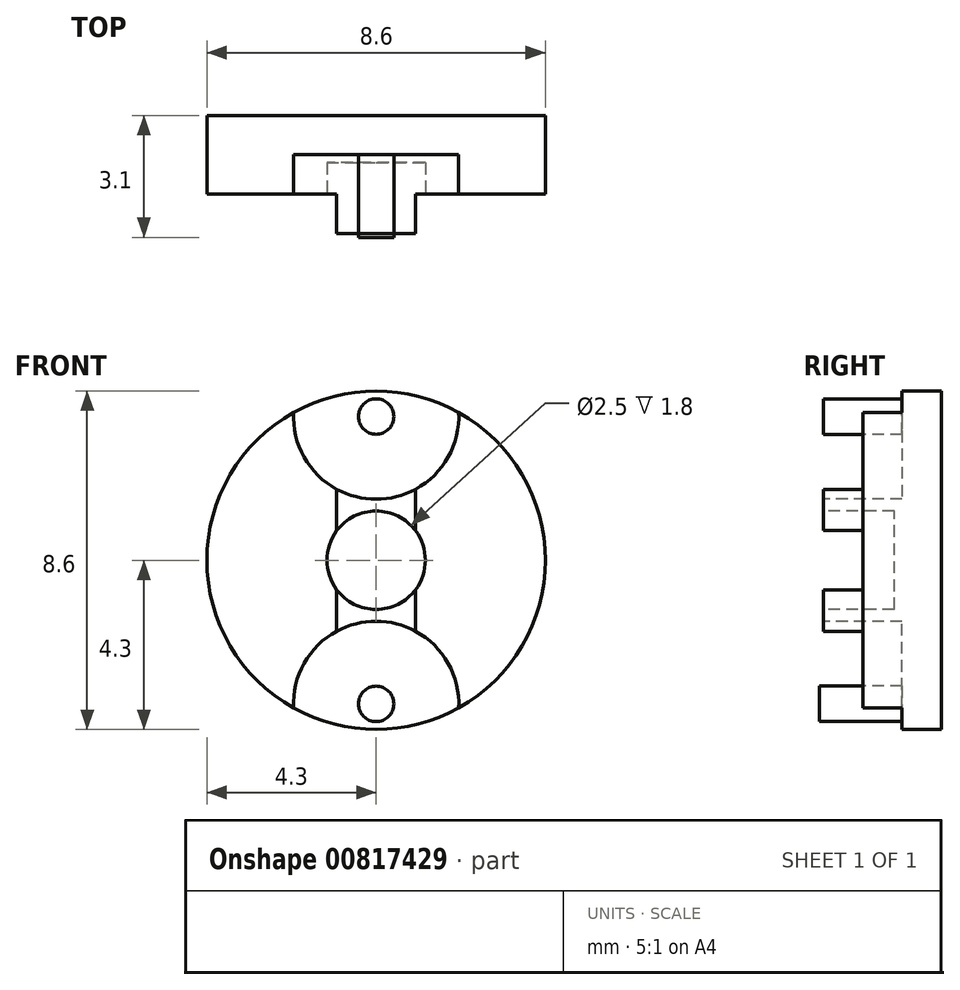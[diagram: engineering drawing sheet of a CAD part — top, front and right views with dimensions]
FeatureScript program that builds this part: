
annotation { "Feature Type Name" : "Feature", "Feature Type Description" : "" }
export const myFeature = defineFeature(function(context is Context, id is Id, definition is map)
    precondition{}
    {
        {
            var Q0;
            Q0=qCreatedBy(makeId("Front.planeOp"),FACE);
            var sketch = newSketch(context, id + "F0", { "sketchPlane" : qUnion([Q0])});
            skCircle(sketch, "E0", {"center": v(0, 0) * mm, "radius": 4.3 * mm});
            skSolve(sketch);
        }
        {
            var Q0;
            Q0=makeQuery(id+"F0.imprint","IMPRINT",FACE,{"disambiguationData":[TD([[makeQuery(id+"F0.imprint","IMPRINT",EDGE,{"derivedFrom":sQuery(id+"F0.wireOp",EDGE,"E0")}),1.0]])]});
            extrude(context, id + "F1", {"entities" : qUnion([Q0]), "depth" : 3 * mm, "offsetDistance" : 25 * mm});
        }
        {
            var Q0;
            Q0=makeQuery(id+"F1.opExtrude","CAP_FACE",FACE,{"disambiguationData":[OSD([sQuery(id+"F0.wireOp",EDGE,"E0")])],"isStart":false});
            var sketch = newSketch(context, id + "F2", { "sketchPlane" : qUnion([Q0])});
            skCircle(sketch, "E1", {"center": v(0, 3.65) * mm, "radius": 2.1 * mm});
            skCircle(sketch, "E2", {"center": v(0, 3.65) * mm, "radius": 0.45 * mm});
            skPoint(sketch, "E3.center", {"position": v(0, 0) * mm});
            skCircle(sketch, "E4.1.0", {"center": v(0, -3.65) * mm, "radius": 0.45 * mm});
            skCircle(sketch, "E4.1.1", {"center": v(0, -3.65) * mm, "radius": 2.1 * mm});
            skLineSegment(sketch, "E5", {"start": v(-2.1, -3.75) * mm, "end": v(-2.1, -3.75) * mm});
            skCircle(sketch, "E6.1.0", {"center": v(0, -3.65) * mm, "radius": 0.75 * mm});
            skLineSegment(sketch, "E7", {"start": v(-1, 4.18) * mm, "end": v(-1, -4.18) * mm});
            skLineSegment(sketch, "E8.MirrorCS", {"start": v(1, 4.18) * mm, "end": v(1, -4.18) * mm});
            skSolve(sketch);
        }
        {
            var Q0;
            Q0=makeQuery(id+"F2.imprint","IMPRINT",FACE,{"disambiguationData":[TD([[makeQuery(id+"F2.imprint","IMPRINT",EDGE,{"derivedFrom":sQuery(id+"F2.wireOp",EDGE,"E4.1.0")}),-1.0]])]});
            var Q1;
            Q1=makeQuery(id+"F2.imprint","IMPRINT",FACE,{"disambiguationData":[TD([[makeQuery(id+"F2.imprint","IMPRINT",EDGE,{"derivedFrom":sQuery(id+"F2.wireOp",EDGE,"E4.2.0")}),-1.0]])]});
            var Q2;
            Q2=makeQuery(id+"F2.imprint","IMPRINT",FACE,{"disambiguationData":[TD([[makeQuery(id+"F2.imprint","IMPRINT",EDGE,{"derivedFrom":sQuery(id+"F2.wireOp",EDGE,"E2")}),-1.0]])]});
            var Q3;
            {var subQ0=sQuery(id+"F2.wireOp",EDGE,"72799f41-8f97-4659-aa58-32a5e735416f.0");var subQ1=sQuery(id+"F2.wireOp",EDGE,"E1");var subQ2=makeQuery(id+"F2.imprint","INTERSECT",VERTEX,{"derivedFrom":[subQ1,subQ0]});Q3=makeQuery(id+"F2.imprint","IMPRINT",FACE,{"disambiguationData":[TD([[makeQuery(id+"F2.imprint","IMPRINT",EDGE,{"disambiguationData":[TD([[subQ2,1.0]])],"derivedFrom":subQ1}),1.0]])]});}
            var Q4;
            {var subQ0=sQuery(id+"F2.wireOp",EDGE,"244a7301-85a8-4d62-895f-e92157d3d9ef.0");var subQ1=sQuery(id+"F2.wireOp",EDGE,"E1");var subQ2=makeQuery(id+"F2.imprint","INTERSECT",VERTEX,{"derivedFrom":[subQ1,subQ0]});Q4=makeQuery(id+"F2.imprint","IMPRINT",FACE,{"disambiguationData":[TD([[makeQuery(id+"F2.imprint","IMPRINT",EDGE,{"disambiguationData":[TD([[subQ2,-1.0]])],"derivedFrom":subQ1}),1.0]])]});}
            var Q5;
            {var subQ0=sQuery(id+"F2.wireOp",EDGE,"244a7301-85a8-4d62-895f-e92157d3d9ef.0");var subQ1=sQuery(id+"F2.wireOp",EDGE,"E4.2.1");var subQ2=makeQuery(id+"F2.imprint","INTERSECT",VERTEX,{"derivedFrom":[subQ1,subQ0]});Q5=makeQuery(id+"F2.imprint","IMPRINT",FACE,{"disambiguationData":[TD([[makeQuery(id+"F2.imprint","IMPRINT",EDGE,{"disambiguationData":[TD([[subQ2,1.0]])],"derivedFrom":subQ1}),1.0]])]});}
            var Q6;
            {var subQ0=sQuery(id+"F2.wireOp",EDGE,"b240cd5d-7871-482e-b949-4fee4bfa505a.0");var subQ1=sQuery(id+"F2.wireOp",EDGE,"E4.2.1");var subQ2=makeQuery(id+"F2.imprint","INTERSECT",VERTEX,{"derivedFrom":[subQ1,subQ0]});Q6=makeQuery(id+"F2.imprint","IMPRINT",FACE,{"disambiguationData":[TD([[makeQuery(id+"F2.imprint","IMPRINT",EDGE,{"disambiguationData":[TD([[subQ2,-1.0]])],"derivedFrom":subQ1}),1.0]])]});}
            var Q7;
            {var subQ0=sQuery(id+"F2.wireOp",EDGE,"b240cd5d-7871-482e-b949-4fee4bfa505a.0");var subQ1=sQuery(id+"F2.wireOp",EDGE,"E4.1.1");var subQ2=makeQuery(id+"F2.imprint","INTERSECT",VERTEX,{"derivedFrom":[subQ1,subQ0]});Q7=makeQuery(id+"F2.imprint","IMPRINT",FACE,{"disambiguationData":[TD([[makeQuery(id+"F2.imprint","IMPRINT",EDGE,{"disambiguationData":[TD([[subQ2,1.0]])],"derivedFrom":subQ1}),1.0]])]});}
            var Q8;
            {var subQ0=sQuery(id+"F2.wireOp",EDGE,"72799f41-8f97-4659-aa58-32a5e735416f.0");var subQ1=sQuery(id+"F2.wireOp",EDGE,"E4.1.1");var subQ2=makeQuery(id+"F2.imprint","INTERSECT",VERTEX,{"derivedFrom":[subQ1,subQ0]});Q8=makeQuery(id+"F2.imprint","IMPRINT",FACE,{"disambiguationData":[TD([[makeQuery(id+"F2.imprint","IMPRINT",EDGE,{"disambiguationData":[TD([[subQ2,-1.0]])],"derivedFrom":subQ1}),1.0]])]});}
            var Q9;
            Q9=makeQuery(id+"F2.imprint","IMPRINT",FACE,{"disambiguationData":[TD([[makeQuery(id+"F2.imprint","IMPRINT",EDGE,{"derivedFrom":sQuery(id+"F2.wireOp",EDGE,"E6.1.0")}),-1.0]])]});
            var Q10;
            Q10=makeQuery(id+"F2.imprint","IMPRINT",FACE,{"disambiguationData":[TD([[makeQuery(id+"F2.imprint","IMPRINT",EDGE,{"derivedFrom":sQuery(id+"F2.wireOp",EDGE,"E6.2.0")}),-1.0]])]});
            var Q11;
            Q11=makeQuery(id+"F2.imprint","IMPRINT",FACE,{"disambiguationData":[TD([[makeQuery(id+"F2.imprint","IMPRINT",EDGE,{"derivedFrom":sQuery(id+"F2.wireOp",EDGE,"HzP3ErbT-1h8t-Fggi-4kVG-w2r0vP4Ld2Wb")}),-1.0]])]});
            var Q12;
            {var subQ0=sQuery(id+"F2.wireOp",EDGE,"b240cd5d-7871-482e-b949-4fee4bfa505a.0");var subQ1=sQuery(id+"F2.wireOp",EDGE,"E4.1.1");var subQ2=makeQuery(id+"F2.imprint","INTERSECT",VERTEX,{"derivedFrom":[subQ1,subQ0]});Q12=makeQuery(id+"F2.imprint","IMPRINT",FACE,{"disambiguationData":[TD([[makeQuery(id+"F2.imprint","IMPRINT",EDGE,{"disambiguationData":[TD([[subQ2,-1.0]])],"derivedFrom":subQ1}),1.0]])]});}
            var Q13;
            {var subQ0=sQuery(id+"F2.wireOp",EDGE,"244a7301-85a8-4d62-895f-e92157d3d9ef.0");var subQ1=sQuery(id+"F2.wireOp",EDGE,"E4.1.1");var subQ2=makeQuery(id+"F2.imprint","INTERSECT",VERTEX,{"derivedFrom":[subQ1,subQ0]});Q13=makeQuery(id+"F2.imprint","IMPRINT",FACE,{"disambiguationData":[TD([[makeQuery(id+"F2.imprint","IMPRINT",EDGE,{"disambiguationData":[TD([[subQ2,1.0]])],"derivedFrom":subQ1}),1.0]])]});}
            extrude(context, id + "F3", {"entities" : qUnion([Q0, Q1, Q2, Q3, Q4, Q5, Q6, Q7, Q8, Q9, Q10, Q11, Q12, Q13]), "operationType" : NewBodyOperationType.REMOVE, "oppositeDirection" : true, "depth" : 2 * mm, "offsetDistance" : 25 * mm});
        }
        {
            var Q0;
            {var subQ0=sQuery(id+"F0.wireOp",EDGE,"E0");Q0=makeQuery(id+"F3.boolean.opBoolean","SPLIT",FACE,{"disambiguationData":[TD([makeQuery(id+"F1.opExtrude","SWEPT_FACE",FACE,{"disambiguationData":[OSD([subQ0])]})])],"derivedFrom":makeQuery(id+"F1.opExtrude","CAP_FACE",FACE,{"disambiguationData":[OSD([subQ0])],"isStart":false})});}
            var sketch = newSketch(context, id + "F4", { "sketchPlane" : qUnion([Q0])});
            skCircle(sketch, "E9", {"center": v(0, 0) * mm, "radius": 1.25 * mm});
            skSolve(sketch);
        }
        {
            var Q0;
            Q0=makeQuery(id+"F4.imprint","IMPRINT",FACE,{"disambiguationData":[TD([[makeQuery(id+"F4.imprint","IMPRINT",EDGE,{"derivedFrom":sQuery(id+"F4.wireOp",EDGE,"E9")}),1.0]])]});
            extrude(context, id + "F5", {"entities" : qUnion([Q0]), "operationType" : NewBodyOperationType.REMOVE, "oppositeDirection" : true, "depth" : 1.8 * mm, "offsetDistance" : 25 * mm});
        }
        {
            var Q0;
            {var subQ0=sQuery(id+"F2.wireOp",EDGE,"E7");var subQ1=sQuery(id+"F2.wireOp",EDGE,"E1");var subQ2=makeQuery(id+"F2.imprint","INTERSECT",VERTEX,{"derivedFrom":[subQ1,subQ0]});Q0=makeQuery(id+"F2.imprint","IMPRINT",FACE,{"disambiguationData":[TD([[makeQuery(id+"F2.imprint","IMPRINT",EDGE,{"disambiguationData":[TD([[subQ2,1.0]])],"derivedFrom":subQ1}),-1.0]])]});}
            var Q1;
            {var subQ0=sQuery(id+"F2.wireOp",EDGE,"E8.MirrorCS");var subQ1=sQuery(id+"F2.wireOp",EDGE,"E1");var subQ2=makeQuery(id+"F2.imprint","INTERSECT",VERTEX,{"derivedFrom":[subQ1,subQ0]});Q1=makeQuery(id+"F2.imprint","IMPRINT",FACE,{"disambiguationData":[TD([[makeQuery(id+"F2.imprint","IMPRINT",EDGE,{"disambiguationData":[TD([[subQ2,-1.0]])],"derivedFrom":subQ1}),-1.0]])]});}
            extrude(context, id + "F6", {"entities" : qUnion([Q0, Q1]), "operationType" : NewBodyOperationType.REMOVE, "oppositeDirection" : true, "depth" : 1 * mm, "offsetDistance" : 25 * mm});
        }
        {
            var Q0;
            Q0=makeQuery(id+"FuLedew03dUDwuD_1.imprint","IMPRINT",FACE,{"disambiguationData":[TD([[makeQuery(id+"FuLedew03dUDwuD_1.imprint","IMPRINT",EDGE,{"derivedFrom":sQuery(id+"FuLedew03dUDwuD_1.wireOp",EDGE,"95fe5a11-708d-4e56-a71e-0591387521810.MirrorC")}),-1.0]])]});
            var Q1;
            Q1=makeQuery(id+"FuLedew03dUDwuD_1.imprint","IMPRINT",FACE,{"disambiguationData":[TD([[makeQuery(id+"FuLedew03dUDwuD_1.imprint","IMPRINT",EDGE,{"derivedFrom":sQuery(id+"FuLedew03dUDwuD_1.wireOp",EDGE,"c3406d6a-d033-4379-a174-ed3e31875f450.MirrorC")}),1.0]])]});
            var Q2;
            Q2=makeQuery(id+"F3.boolean.opBoolean","SPLIT",FACE,{"disambiguationData":[TD([makeQuery(id+"F3.opExtrude","SWEPT_FACE",FACE,{"disambiguationData":[OSD([sQuery(id+"F2.wireOp",EDGE,"E4.1.0")])]})])],"derivedFrom":makeQuery(id+"F1.opExtrude","CAP_FACE",FACE,{"disambiguationData":[OSD([sQuery(id+"F0.wireOp",EDGE,"E0")])],"isStart":false})});
            extrude(context, id + "F7", {"entities" : qUnion([Q0, Q1, Q2]), "operationType" : NewBodyOperationType.ADD, "depth" : 0.1 * mm, "offsetDistance" : 25 * mm});
        }
    });
